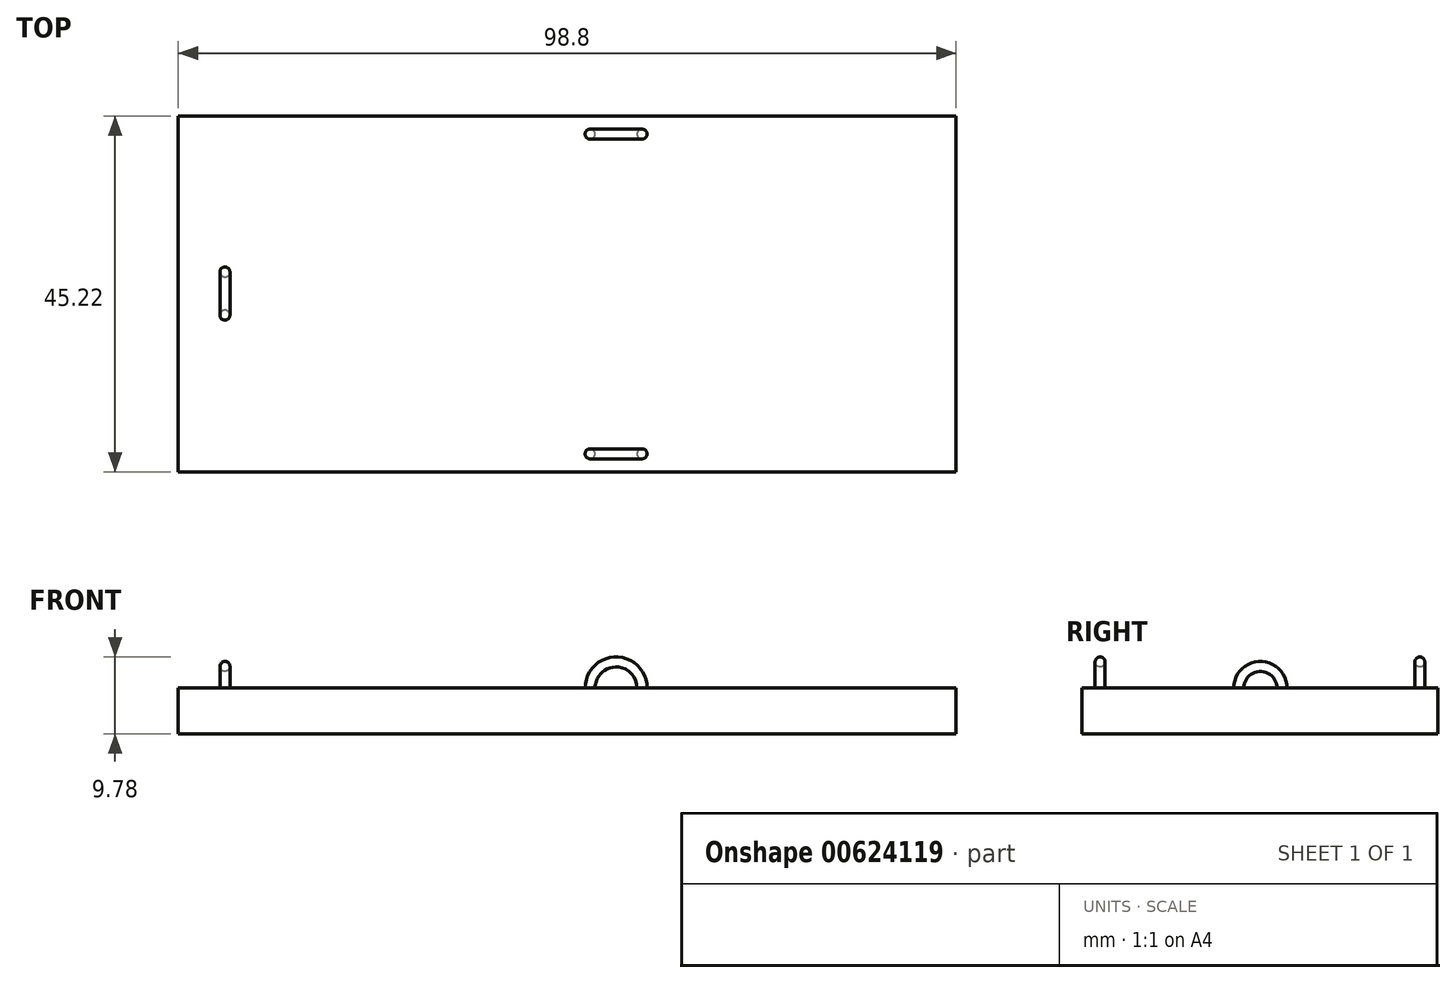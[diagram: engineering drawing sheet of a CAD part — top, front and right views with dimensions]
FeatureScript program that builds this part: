
annotation { "Feature Type Name" : "Feature", "Feature Type Description" : "" }
export const myFeature = defineFeature(function(context is Context, id is Id, definition is map)
    precondition{}
    {
        {
            var Q0;
            Q0=qCreatedBy(makeId("Top.planeOp"),FACE);
            var sketch = newSketch(context, id + "F0", { "sketchPlane" : qUnion([Q0])});
            skLineSegment(sketch, "E0.bottom", {"start": v(-49.4, -22.6) * mm, "end": v(49.4, -22.6) * mm});
            skLineSegment(sketch, "E0.top", {"start": v(-49.4, 22.6) * mm, "end": v(49.4, 22.6) * mm});
            skLineSegment(sketch, "E0.left", {"start": v(-49.4, -22.6) * mm, "end": v(-49.4, 22.6) * mm});
            skLineSegment(sketch, "E0.right", {"start": v(49.4, -22.6) * mm, "end": v(49.4, 22.6) * mm});
            skPoint(sketch, "E0.middle", {"position": v(0, 0) * mm});
            skSolve(sketch);
        }
        {
            var Q0;
            Q0 = qSketchRegion(id + "F0", true);
            extrude(context, id + "F1", {"entities" : qUnion([Q0]), "endBound" : BoundingType.SYMMETRIC, "depth" : 5.84 * mm, "offsetDistance" : 25.4 * mm});
        }
        {
            var Q0;
            Q0=makeQuery(id+"F1.opExtrude","CAP_FACE",FACE,{"disambiguationData":[OSD([sQuery(id+"F0.wireOp",EDGE,"E0.bottom"),sQuery(id+"F0.wireOp",EDGE,"E0.top"),sQuery(id+"F0.wireOp",EDGE,"E0.left"),sQuery(id+"F0.wireOp",EDGE,"E0.right")])],"isStart":false});
            var sketch = newSketch(context, id + "F2", { "sketchPlane" : qUnion([Q0])});
            skCircle(sketch, "E1", {"center": v(-43.48, 2.8) * mm, "radius": 0.64 * mm});
            skCircle(sketch, "E2", {"center": v(-43.48, -2.7) * mm, "radius": 0.64 * mm});
            skLineSegment(sketch, "E3", {"start": v(-43.48, -2.7) * mm, "end": v(-43.48, 2.8) * mm});
            skLineSegment(sketch, "E4", {"start": v(-42.68, 0.05) * mm, "end": v(-44.62, 0.05) * mm});
            skPoint(sketch, "E4.startSnap0", {"position": v(-43.48, 0.05) * mm});
            skSolve(sketch);
        }
        {
            var Q0;
            Q0=makeQuery(id+"F2.imprint","IMPRINT",FACE,{"disambiguationData":[TD([[makeQuery(id+"F2.imprint","IMPRINT",EDGE,{"derivedFrom":sQuery(id+"F2.wireOp",EDGE,"E1")}),1.0]])]});
            var Q1;
            Q1=makeQuery(id+"F2.imprint","IMPRINT",FACE,{"disambiguationData":[TD([[makeQuery(id+"F2.imprint","IMPRINT",EDGE,{"derivedFrom":sQuery(id+"F2.wireOp",EDGE,"E2")}),1.0]])]});
            var Q2;
            Q2=sQuery(id+"F2.wireOp",EDGE,"E4");
            revolve(context, id + "F3", {"operationType" : NewBodyOperationType.ADD, "entities" : qUnion([Q0, Q1]), "axis" : qUnion([Q2]), "revolveType" : RevolveType.ONE_DIRECTION, "angle" : 180 * degree});
        }
        {
            var Q0;
            Q0=makeQuery(id+"F1.opExtrude","CAP_FACE",FACE,{"disambiguationData":[OSD([sQuery(id+"F0.wireOp",EDGE,"E0.bottom"),sQuery(id+"F0.wireOp",EDGE,"E0.top"),sQuery(id+"F0.wireOp",EDGE,"E0.left"),sQuery(id+"F0.wireOp",EDGE,"E0.right")])],"isStart":false});
            var sketch = newSketch(context, id + "F4", { "sketchPlane" : qUnion([Q0])});
            skLineSegment(sketch, "E5", {"start": v(20.2, 7.37) * mm, "end": v(20.2, -7.37) * mm});
            skLineSegment(sketch, "E6", {"start": v(2.9, 0) * mm, "end": v(28.81, 0) * mm});
            skCircle(sketch, "E7", {"center": v(20.2, -7.37) * mm, "radius": 0.64 * mm});
            skCircle(sketch, "E8", {"center": v(20.2, 7.37) * mm, "radius": 0.64 * mm});
            skSolve(sketch);
        }
        {
            var Q0;
            Q0 = qSketchRegion(id + "F4", true);
            var Q1;
            Q1=sQuery(id+"F4.wireOp",EDGE,"E8");
            var Q2;
            Q2=sQuery(id+"F4.wireOp",EDGE,"E6");
            revolve(context, id + "F5", {"bodyType" : ToolBodyType.SURFACE, "entities" : qUnion([Q0]), "surfaceEntities" : qUnion([Q1]), "axis" : qUnion([Q2]), "revolveType" : RevolveType.TWO_DIRECTIONS, "angle" : 180 * degree, "angleBack" : 330 * degree});
        }
        {
            var Q0;
            Q0=makeQuery(id+"F1.opExtrude","CAP_FACE",FACE,{"disambiguationData":[OSD([sQuery(id+"F0.wireOp",EDGE,"E0.bottom"),sQuery(id+"F0.wireOp",EDGE,"E0.top"),sQuery(id+"F0.wireOp",EDGE,"E0.left"),sQuery(id+"F0.wireOp",EDGE,"E0.right")])],"isStart":false});
            var sketch = newSketch(context, id + "F6", { "sketchPlane" : qUnion([Q0])});
            skCircle(sketch, "E9", {"center": v(2.92, -20.3) * mm, "radius": 0.64 * mm});
            skCircle(sketch, "E10", {"center": v(9.53, -20.3) * mm, "radius": 0.64 * mm});
            skLineSegment(sketch, "E11", {"start": v(2.92, -20.3) * mm, "end": v(9.53, -20.3) * mm});
            skLineSegment(sketch, "E12", {"start": v(6.22, -20.3) * mm, "end": v(6.22, -21.53) * mm});
            skLineSegment(sketch, "E13", {"start": v(6.22, -21.53) * mm, "end": v(6.22, -19.06) * mm});
            skLineSegment(sketch, "E14", {"start": v(-49.4, 0) * mm, "end": v(49.4, 0) * mm});
            skCircle(sketch, "E15.MirrorC", {"center": v(2.92, 20.3) * mm, "radius": 0.64 * mm});
            skCircle(sketch, "E16.MirrorC", {"center": v(9.53, 20.3) * mm, "radius": 0.64 * mm});
            skLineSegment(sketch, "E17.MirrorCS", {"start": v(2.92, 20.3) * mm, "end": v(9.53, 20.3) * mm});
            skLineSegment(sketch, "E18.MirrorCS", {"start": v(6.22, 21.53) * mm, "end": v(6.22, 19.06) * mm});
            skSolve(sketch);
        }
        {
            var Q0;
            Q0 = qSketchRegion(id + "F6", true);
            var Q1;
            Q1=sQuery(id+"F6.wireOp",EDGE,"E13");
            revolve(context, id + "F7", {"operationType" : NewBodyOperationType.ADD, "entities" : qUnion([Q0]), "axis" : qUnion([Q1]), "revolveType" : RevolveType.FULL});
        }
    });
